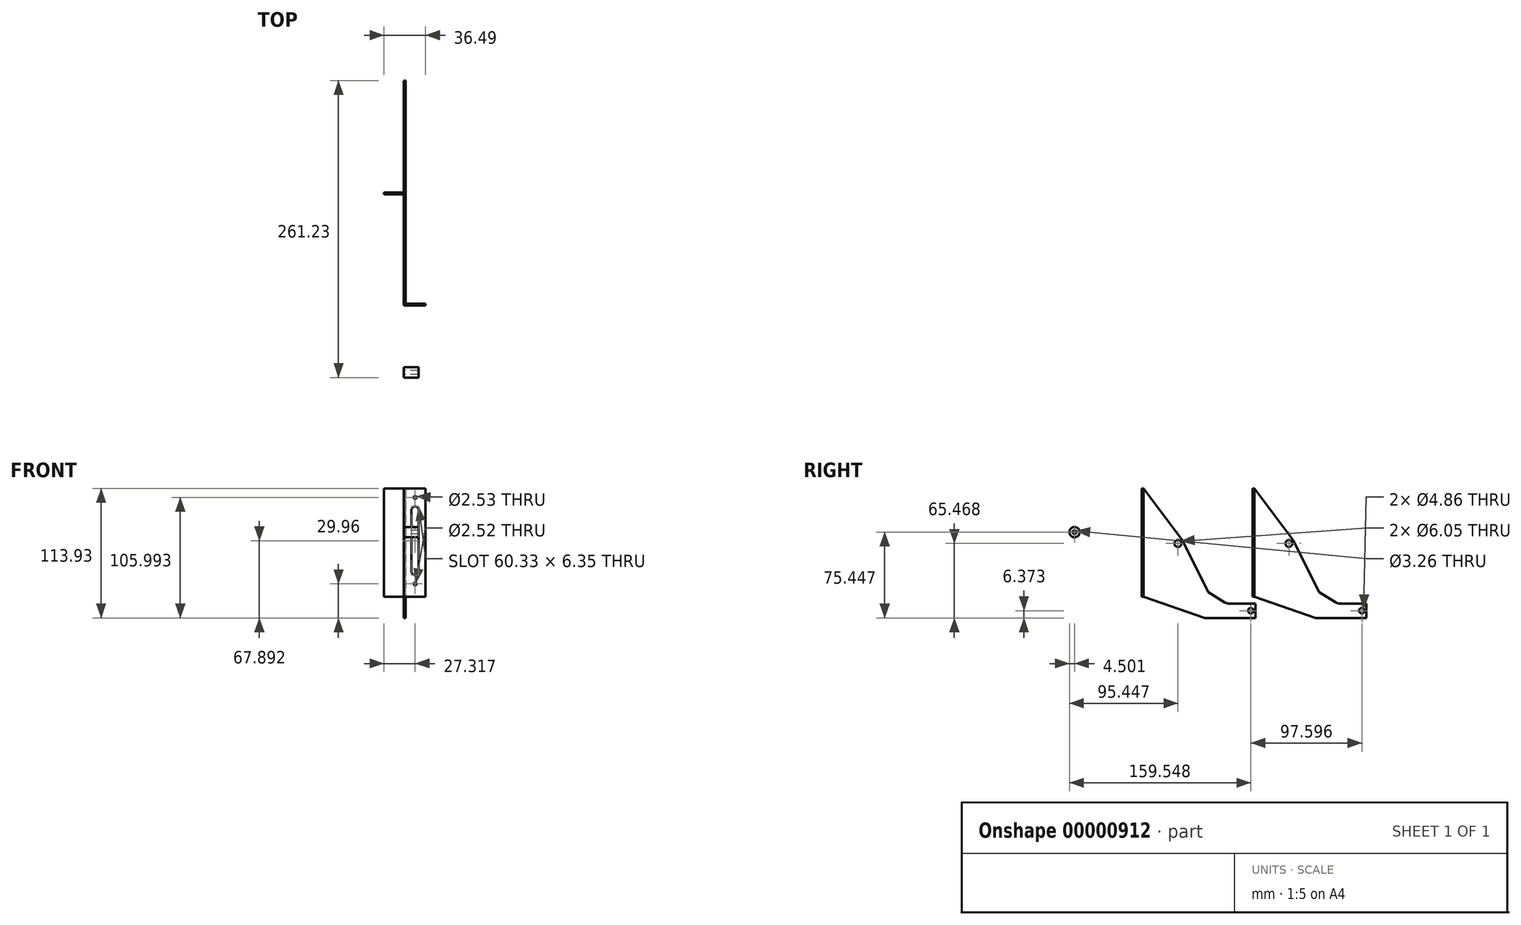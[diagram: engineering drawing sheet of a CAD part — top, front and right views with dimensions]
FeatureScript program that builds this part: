
annotation { "Feature Type Name" : "Feature", "Feature Type Description" : "" }
export const myFeature = defineFeature(function(context is Context, id is Id, definition is map)
    precondition{}
    {
        {
            var Q0;
            Q0=qCreatedBy(makeId("Right.planeOp"),FACE);
            var sketch = newSketch(context, id + "F0", { "sketchPlane" : qUnion([Q0])});
            skLineSegment(sketch, "E0", {"start": v(-0.29, 95.25) * mm, "end": v(0, 95.25) * mm});
            skLineSegment(sketch, "E1", {"start": v(1.59, 0) * mm, "end": v(55.6, -18.68) * mm});
            skLineSegment(sketch, "E2", {"start": v(55.6, -18.68) * mm, "end": v(100.05, -18.68) * mm});
            skLineSegment(sketch, "E3", {"start": v(100.05, -18.68) * mm, "end": v(100.05, -5.98) * mm});
            skLineSegment(sketch, "E4", {"start": v(100.05, -5.98) * mm, "end": v(76.45, -5.98) * mm});
            skLineSegment(sketch, "E5", {"start": v(73.12, -5.04) * mm, "end": v(58.43, 4) * mm});
            skLineSegment(sketch, "E6", {"start": v(58.43, 4) * mm, "end": v(35.88, 49.53) * mm});
            skLineSegment(sketch, "E7", {"start": v(35.88, 49.53) * mm, "end": v(1.59, 95.25) * mm});
            skLineSegment(sketch, "E8", {"start": v(1.59, 95.25) * mm, "end": v(0, 95.25) * mm});
            skLineSegment(sketch, "E9", {"start": v(1.59, 95.25) * mm, "end": v(1.59, 0) * mm});
            skLineSegment(sketch, "E10", {"start": v(0, 95.25) * mm, "end": v(0, 0) * mm});
            skLineSegment(sketch, "E11", {"start": v(1.59, 0) * mm, "end": v(0, 0) * mm});
            skPoint(sketch, "E12.visualSharp", {"position": v(55.6, -18.68) * mm});
            skLineSegment(sketch, "E12.filletArc", {"start": v(55.6, -18.68) * mm, "end": v(55.6, -18.68) * mm});
            skPoint(sketch, "E13.visualSharp", {"position": v(74.65, -5.98) * mm});
            skArc(sketch, "E13.filletArc", {"start": v(73.12, -5.04) * mm, "mid": v(74.72, -5.74) * mm, "end": v(76.45, -5.98) * mm});
            skCircle(sketch, "E14", {"center": v(95.97, -12.3) * mm, "radius": 2.43 * mm});
            skCircle(sketch, "E15", {"center": v(31.87, 46.79) * mm, "radius": 3.03 * mm});
            skSolve(sketch);
        }
        {
            var Q0;
            Q0=qCreatedBy(makeId("Right.planeOp"),FACE);
            var sketch = newSketch(context, id + "F1", { "sketchPlane" : qUnion([Q0])});
            skCircle(sketch, "E16", {"center": v(-59.08, 56.77) * mm, "radius": 4.5 * mm});
            skCircle(sketch, "E17", {"center": v(-59.08, 56.77) * mm, "radius": 1.63 * mm});
            skSolve(sketch);
        }
        {
            var Q0;
            Q0=makeQuery(id+"F1.imprint","IMPRINT",FACE,{"disambiguationData":[TD([[makeQuery(id+"F1.imprint","IMPRINT",EDGE,{"derivedFrom":sQuery(id+"F1.wireOp",EDGE,"E16")}),1.0]])]});
            extrude(context, id + "F2", {"entities" : qUnion([Q0]), "depth" : 13 * mm});
        }
        {
            var Q0;
            Q0=makeQuery(id+"F0.imprint","IMPRINT",FACE,{"disambiguationData":[TD([[makeQuery(id+"F0.imprint","IMPRINT",EDGE,{"derivedFrom":sQuery(id+"F0.wireOp",EDGE,"E1")}),1.0]])]});
            extrude(context, id + "F3", {"entities" : qUnion([Q0]), "depth" : 1.59 * mm});
        }
        {
            var Q0;
            Q0=makeQuery(id+"F0.imprint","IMPRINT",FACE,{"disambiguationData":[TD([[makeQuery(id+"F0.imprint","IMPRINT",EDGE,{"derivedFrom":sQuery(id+"F0.wireOp",EDGE,"E8")}),1.0]])]});
            extrude(context, id + "F4", {"entities" : qUnion([Q0]), "operationType" : NewBodyOperationType.ADD, "depth" : 19.05 * mm});
        }
        {
            var Q0;
            Q0=makeQuery(id+"F4.opExtrude","SWEPT_FACE",FACE,{"disambiguationData":[OSD([sQuery(id+"F0.wireOp",EDGE,"E10")])]});
            var sketch = newSketch(context, id + "F5", { "sketchPlane" : qUnion([Q0])});
            skLineSegment(sketch, "E18.bottom", {"start": v(9.88, 79.37) * mm, "end": v(9.88, 79.37) * mm});
            skLineSegment(sketch, "E18.top", {"start": v(9.88, 19.05) * mm, "end": v(9.88, 19.05) * mm});
            skLineSegment(sketch, "E18.left", {"start": v(6.7, 76.2) * mm, "end": v(6.7, 22.22) * mm});
            skLineSegment(sketch, "E18.right", {"start": v(13.05, 76.2) * mm, "end": v(13.05, 22.22) * mm});
            skPoint(sketch, "E19.visualSharp", {"position": v(6.7, 79.37) * mm});
            skArc(sketch, "E19.filletArc", {"start": v(9.88, 79.37) * mm, "mid": v(7.63, 78.45) * mm, "end": v(6.7, 76.2) * mm});
            skPoint(sketch, "E20.visualSharp", {"position": v(13.05, 79.37) * mm});
            skArc(sketch, "E20.filletArc", {"start": v(13.05, 76.2) * mm, "mid": v(12.12, 78.45) * mm, "end": v(9.88, 79.37) * mm});
            skPoint(sketch, "E21.visualSharp", {"position": v(6.7, 19.05) * mm});
            skArc(sketch, "E21.filletArc", {"start": v(6.7, 22.22) * mm, "mid": v(7.63, 19.98) * mm, "end": v(9.88, 19.05) * mm});
            skPoint(sketch, "E22.visualSharp", {"position": v(13.05, 19.05) * mm});
            skArc(sketch, "E22.filletArc", {"start": v(9.88, 19.05) * mm, "mid": v(12.12, 19.98) * mm, "end": v(13.05, 22.22) * mm});
            skCircle(sketch, "E23", {"center": v(9.88, 87.31) * mm, "radius": 1.26 * mm});
            skCircle(sketch, "E24", {"center": v(9.88, 11.28) * mm, "radius": 1.26 * mm});
            skSolve(sketch);
        }
        {
            var Q0;
            Q0 = qSketchRegion(id + "F5", true);
            extrude(context, id + "F6", {"entities" : qUnion([Q0]), "operationType" : NewBodyOperationType.REMOVE, "endBound" : BoundingType.THROUGH_ALL, "oppositeDirection" : true, "depth" : 0.25 * mm});
        }
        {
            var Q0;
            Q0=makeQuery(id+"F3.opExtrude","SWEPT_BODY",BODY,{"disambiguationData":[OSD([sQuery(id+"F0.wireOp",EDGE,"E1"),sQuery(id+"F0.wireOp",EDGE,"E2"),sQuery(id+"F0.wireOp",EDGE,"E3"),sQuery(id+"F0.wireOp",EDGE,"E4"),sQuery(id+"F0.wireOp",EDGE,"E5"),sQuery(id+"F0.wireOp",EDGE,"E6"),sQuery(id+"F0.wireOp",EDGE,"E7"),sQuery(id+"F0.wireOp",EDGE,"E9"),sQuery(id+"F0.wireOp",EDGE,"E13.filletArc"),sQuery(id+"F0.wireOp",EDGE,"E14"),sQuery(id+"F0.wireOp",EDGE,"E15")])]});
            transform(context, id + "F7", {"entities" : qUnion([Q0]), "transformType" : TransformType.COPY, "oppositeX" : false, "oppositeY" : false, "oppositeZ" : false});
        }
        {
            var Q0;
            Q0=makeQuery(id+"F3.opExtrude","SWEPT_BODY",BODY,{"disambiguationData":[OSD([sQuery(id+"F0.wireOp",EDGE,"E1"),sQuery(id+"F0.wireOp",EDGE,"E2"),sQuery(id+"F0.wireOp",EDGE,"E3"),sQuery(id+"F0.wireOp",EDGE,"E4"),sQuery(id+"F0.wireOp",EDGE,"E5"),sQuery(id+"F0.wireOp",EDGE,"E6"),sQuery(id+"F0.wireOp",EDGE,"E7"),sQuery(id+"F0.wireOp",EDGE,"E9"),sQuery(id+"F0.wireOp",EDGE,"E13.filletArc"),sQuery(id+"F0.wireOp",EDGE,"E14"),sQuery(id+"F0.wireOp",EDGE,"E15")])]});
            transform(context, id + "F8", {"entities" : qUnion([Q0]), "transformType" : TransformType.TRANSLATION_3D, "dx" : 0 * mm, "dy" : 97.6 * mm, "dz" : 0 * mm, "makeCopy" : false});
        }
        {
            var Q0;
            Q0=makeQuery(id+"F4.opExtrude","CAP_FACE",FACE,{"disambiguationData":[OSD([sQuery(id+"F0.wireOp",EDGE,"E8"),sQuery(id+"F0.wireOp",EDGE,"E9"),sQuery(id+"F0.wireOp",EDGE,"E10"),sQuery(id+"F0.wireOp",EDGE,"E11")])],"isStart":false});
            extrude(context, id + "F9", {"entities" : qUnion([Q0]), "operationType" : NewBodyOperationType.REMOVE, "oppositeDirection" : true, "depth" : 17.44 * mm});
        }
        {
            var Q0;
            Q0=makeQuery(id+"F9.boolean.opBoolean","COPY",FACE,{"derivedFrom":makeQuery(id+"F9.opExtrude","CAP_FACE",FACE,{"disambiguationData":[OSD([sQuery(id+"F0.wireOp",EDGE,"E8"),sQuery(id+"F0.wireOp",EDGE,"E9"),sQuery(id+"F0.wireOp",EDGE,"E10"),sQuery(id+"F0.wireOp",EDGE,"E11")])],"isStart":false})});
            extrude(context, id + "F10", {"entities" : qUnion([Q0]), "operationType" : NewBodyOperationType.ADD, "oppositeDirection" : true, "depth" : 19.05 * mm});
        }
        {
            var Q0;
            Q0=makeQuery(id+"F10.opExtrude","SWEPT_FACE",FACE,{"disambiguationData":[OSD([sQuery(id+"F0.wireOp",EDGE,"E9")])]});
            var sketch = newSketch(context, id + "F11", { "sketchPlane" : qUnion([Q0])});
            skLineSegment(sketch, "E25.bottom", {"start": v(7.91, 76.2) * mm, "end": v(7.91, 76.2) * mm});
            skLineSegment(sketch, "E25.top", {"start": v(7.91, 15.87) * mm, "end": v(7.91, 15.87) * mm});
            skLineSegment(sketch, "E25.left", {"start": v(4.74, 73.03) * mm, "end": v(4.74, 19.05) * mm});
            skLineSegment(sketch, "E25.right", {"start": v(11.09, 73.02) * mm, "end": v(11.09, 19.05) * mm});
            skPoint(sketch, "E26.visualSharp", {"position": v(4.74, 76.2) * mm});
            skArc(sketch, "E26.filletArc", {"start": v(7.91, 76.2) * mm, "mid": v(5.67, 75.27) * mm, "end": v(4.74, 73.03) * mm});
            skPoint(sketch, "E27.visualSharp", {"position": v(11.09, 76.2) * mm});
            skArc(sketch, "E27.filletArc", {"start": v(11.09, 73.02) * mm, "mid": v(10.16, 75.27) * mm, "end": v(7.91, 76.2) * mm});
            skPoint(sketch, "E28.visualSharp", {"position": v(4.74, 15.87) * mm});
            skArc(sketch, "E28.filletArc", {"start": v(4.74, 19.05) * mm, "mid": v(5.67, 16.8) * mm, "end": v(7.91, 15.87) * mm});
            skPoint(sketch, "E29.visualSharp", {"position": v(11.09, 15.87) * mm});
            skArc(sketch, "E29.filletArc", {"start": v(7.91, 15.87) * mm, "mid": v(10.16, 16.8) * mm, "end": v(11.09, 19.05) * mm});
            skSolve(sketch);
        }
        {
            var Q0;
            Q0=makeQuery(id+"F11.imprint","IMPRINT",FACE,{"disambiguationData":[TD([[makeQuery(id+"F11.imprint","IMPRINT",EDGE,{"derivedFrom":sQuery(id+"F11.wireOp",EDGE,"E25.left")}),1.0]])]});
            extrude(context, id + "F12", {"entities" : qUnion([Q0]), "operationType" : NewBodyOperationType.REMOVE, "oppositeDirection" : true, "depth" : 25.4 * mm});
        }
    });
